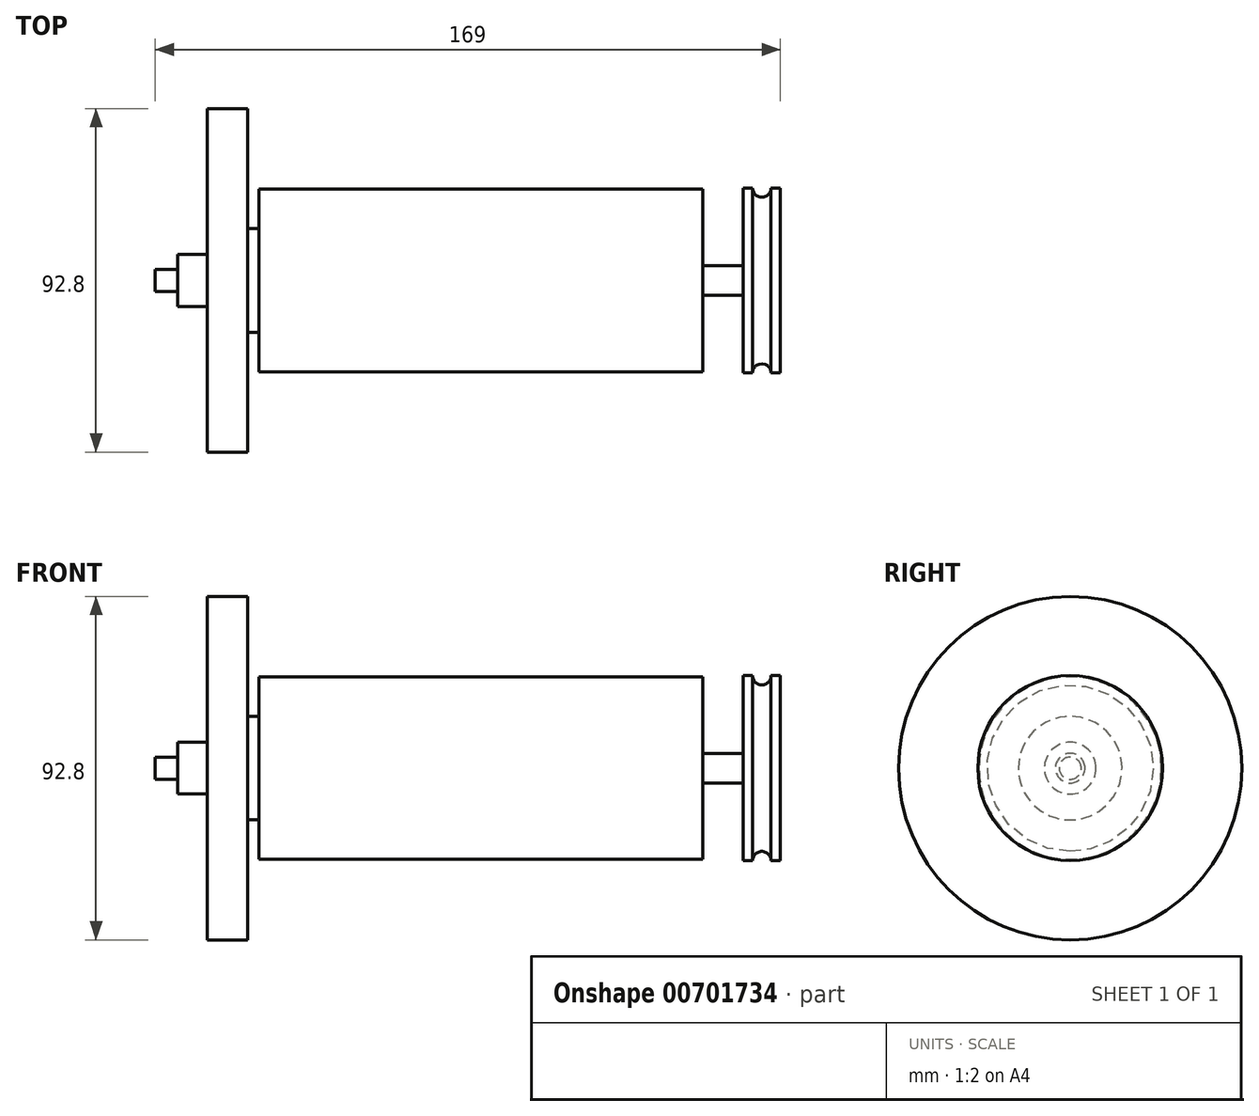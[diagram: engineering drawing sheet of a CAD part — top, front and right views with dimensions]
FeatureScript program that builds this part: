
annotation { "Feature Type Name" : "Feature", "Feature Type Description" : "" }
export const myFeature = defineFeature(function(context is Context, id is Id, definition is map)
    precondition{}
    {
        {
            var Q0;
            Q0=qCreatedBy(makeId("Right.planeOp"),FACE);
            var sketch = newSketch(context, id + "F0", { "sketchPlane" : qUnion([Q0])});
            skCircle(sketch, "E0", {"center": v(0, 0) * mm, "radius": 24.65 * mm});
            skSolve(sketch);
        }
        {
            var Q0;
            Q0=qSketchRegion(id+"F0",true);
            extrude(context, id + "F1", {"entities" : qUnion([Q0]), "depth" : 120 * mm, "offsetDistance" : 25.4 * mm});
        }
        {
            var Q0;
            Q0=makeQuery(id+"F1.opExtrude","CAP_FACE",FACE,{"disambiguationData":[OSD([sQuery(id+"F0.wireOp",EDGE,"E0")])],"isStart":false});
            var sketch = newSketch(context, id + "F2", { "sketchPlane" : qUnion([Q0])});
            skCircle(sketch, "E1", {"center": v(0, 0) * mm, "radius": 4 * mm});
            skSolve(sketch);
        }
        {
            var Q0;
            Q0=qSketchRegion(id+"F2",true);
            extrude(context, id + "F3", {"entities" : qUnion([Q0]), "operationType" : NewBodyOperationType.ADD, "depth" : 21 * mm, "offsetDistance" : 25.4 * mm});
        }
        {
            var Q0;
            Q0=makeQuery(id+"F1.opExtrude","CAP_FACE",FACE,{"disambiguationData":[OSD([sQuery(id+"F0.wireOp",EDGE,"E0")])],"isStart":true});
            var sketch = newSketch(context, id + "F4", { "sketchPlane" : qUnion([Q0])});
            skCircle(sketch, "E2", {"center": v(0, 0) * mm, "radius": 14 * mm});
            skSolve(sketch);
        }
        {
            var Q0;
            Q0=makeQuery(id+"F4.imprint","IMPRINT",FACE,{"disambiguationData":[TD([[makeQuery(id+"F4.imprint","IMPRINT",EDGE,{"derivedFrom":sQuery(id+"F4.wireOp",EDGE,"E2")}),1.0]])]});
            extrude(context, id + "F5", {"entities" : qUnion([Q0]), "operationType" : NewBodyOperationType.ADD, "depth" : 3 * mm, "offsetDistance" : 25.4 * mm});
        }
        {
            var Q0;
            Q0=makeQuery(id+"F5.opExtrude","CAP_FACE",FACE,{"disambiguationData":[OSD([sQuery(id+"F4.wireOp",EDGE,"E2")])],"isStart":false});
            var sketch = newSketch(context, id + "F6", { "sketchPlane" : qUnion([Q0])});
            skCircle(sketch, "E3", {"center": v(0, 0) * mm, "radius": 46.4 * mm});
            skSolve(sketch);
        }
        {
            var Q0;
            Q0=makeQuery(id+"F6.imprint","IMPRINT",FACE,{"disambiguationData":[TD([[makeQuery(id+"F6.imprint","IMPRINT",EDGE,{"derivedFrom":sQuery(id+"F6.wireOp",EDGE,"E3")}),1.0]])]});
            var Q1;
            Q1=makeQuery(id+"F6.imprint","IMPRINT",FACE,{"disambiguationData":[TD([[makeQuery(id+"F6.imprint","IMPRINT",EDGE,{"derivedFrom":makeQuery(id+"F5.opExtrude","CAP_EDGE",EDGE,{"disambiguationData":[OSD([sQuery(id+"F4.wireOp",EDGE,"E2")])],"isStart":false})}),1.0]])]});
            extrude(context, id + "F7", {"entities" : qUnion([Q0, Q1]), "depth" : 11 * mm, "offsetDistance" : 25.4 * mm});
        }
        {
            var Q0;
            Q0=makeQuery(id+"F7.opExtrude","CAP_FACE",FACE,{"disambiguationData":[OSD([sQuery(id+"F6.wireOp",EDGE,"E3")])],"isStart":false});
            var sketch = newSketch(context, id + "F8", { "sketchPlane" : qUnion([Q0])});
            skCircle(sketch, "E4", {"center": v(0, 0) * mm, "radius": 7 * mm});
            skSolve(sketch);
        }
        {
            var Q0;
            Q0=makeQuery(id+"F8.imprint","IMPRINT",FACE,{"disambiguationData":[TD([[makeQuery(id+"F8.imprint","IMPRINT",EDGE,{"derivedFrom":sQuery(id+"F8.wireOp",EDGE,"E4")}),1.0]])]});
            extrude(context, id + "F9", {"entities" : qUnion([Q0]), "operationType" : NewBodyOperationType.ADD, "depth" : 8 * mm, "offsetDistance" : 25.4 * mm});
        }
        {
            var Q0;
            Q0=makeQuery(id+"F9.opExtrude","CAP_FACE",FACE,{"disambiguationData":[OSD([sQuery(id+"F8.wireOp",EDGE,"E4")])],"isStart":false});
            var sketch = newSketch(context, id + "F10", { "sketchPlane" : qUnion([Q0])});
            skCircle(sketch, "E5", {"center": v(0, 0) * mm, "radius": 3 * mm});
            skSolve(sketch);
        }
        {
            var Q0;
            Q0=makeQuery(id+"F10.imprint","IMPRINT",FACE,{"disambiguationData":[TD([[makeQuery(id+"F10.imprint","IMPRINT",EDGE,{"derivedFrom":sQuery(id+"F10.wireOp",EDGE,"E5")}),1.0]])]});
            extrude(context, id + "F11", {"entities" : qUnion([Q0]), "operationType" : NewBodyOperationType.ADD, "depth" : 6 * mm, "offsetDistance" : 25.4 * mm});
        }
        {
            var Q0;
            Q0=makeQuery(id+"F3.opExtrude","CAP_FACE",FACE,{"disambiguationData":[OSD([sQuery(id+"F2.wireOp",EDGE,"E1")])],"isStart":false});
            var sketch = newSketch(context, id + "F12", { "sketchPlane" : qUnion([Q0])});
            skArc(sketch, "E6", {"start": v(-4, 0) * mm, "mid": v(0, -4) * mm, "end": v(4, 0) * mm});
            skArc(sketch, "E7", {"start": v(-25, 0) * mm, "mid": v(0, -25) * mm, "end": v(25, 0) * mm});
            skLineSegment(sketch, "E8.trimOffspring", {"start": v(4, 0) * mm, "end": v(25, 0) * mm});
            skLineSegment(sketch, "E9", {"start": v(-4, 0) * mm, "end": v(-25, 0) * mm});
            skSolve(sketch);
        }
        {
            var Q0;
            Q0=makeQuery(id+"F12.imprint","IMPRINT",FACE,{"disambiguationData":[TD([[makeQuery(id+"F12.imprint","IMPRINT",EDGE,{"derivedFrom":sQuery(id+"F12.wireOp",EDGE,"E6")}),-1.0]])]});
            extrude(context, id + "F13", {"entities" : qUnion([Q0]), "oppositeDirection" : true, "depth" : 10 * mm, "offsetDistance" : 25 * mm});
        }
        {
            var Q0;
            Q0=qCreatedBy(makeId("Top.planeOp"),FACE);
            var sketch = newSketch(context, id + "F14", { "sketchPlane" : qUnion([Q0])});
            skLineSegment(sketch, "E10", {"start": v(0, 0) * mm, "end": v(502.96, 0) * mm});
            skSolve(sketch);
        }
        {
            var Q0;
            Q0=qCreatedBy(makeId("Top.planeOp"),FACE);
            var sketch = newSketch(context, id + "F15", { "sketchPlane" : qUnion([Q0])});
            skCircle(sketch, "E11", {"center": v(136, 25) * mm, "radius": 2.5 * mm});
            skSolve(sketch);
        }
        {
            var Q0;
            Q0=qSketchRegion(id+"F15",true);
            var Q1;
            Q1=sQuery(id+"F14.wireOp",EDGE,"E10");
            revolve(context, id + "F16", {"operationType" : NewBodyOperationType.REMOVE, "entities" : qUnion([Q0]), "axis" : qUnion([Q1]), "revolveType" : RevolveType.FULL});
        }
        {
            var Q0;
            Q0=makeQuery(id+"F13.opExtrude","SWEPT_BODY",BODY,{"disambiguationData":[OSD([sQuery(id+"F12.wireOp",EDGE,"E6"),sQuery(id+"F12.wireOp",EDGE,"E7"),sQuery(id+"F12.wireOp",EDGE,"E8.trimOffspring"),sQuery(id+"F12.wireOp",EDGE,"E9")])]});
            var Q1;
            Q1=qCreatedBy(makeId("Top.planeOp"),FACE);
            mirror(context, id + "F17", {"operationType" : NewBodyOperationType.ADD, "entities" : qUnion([Q0]), "mirrorPlane" : qUnion([Q1])});
        }
    });
